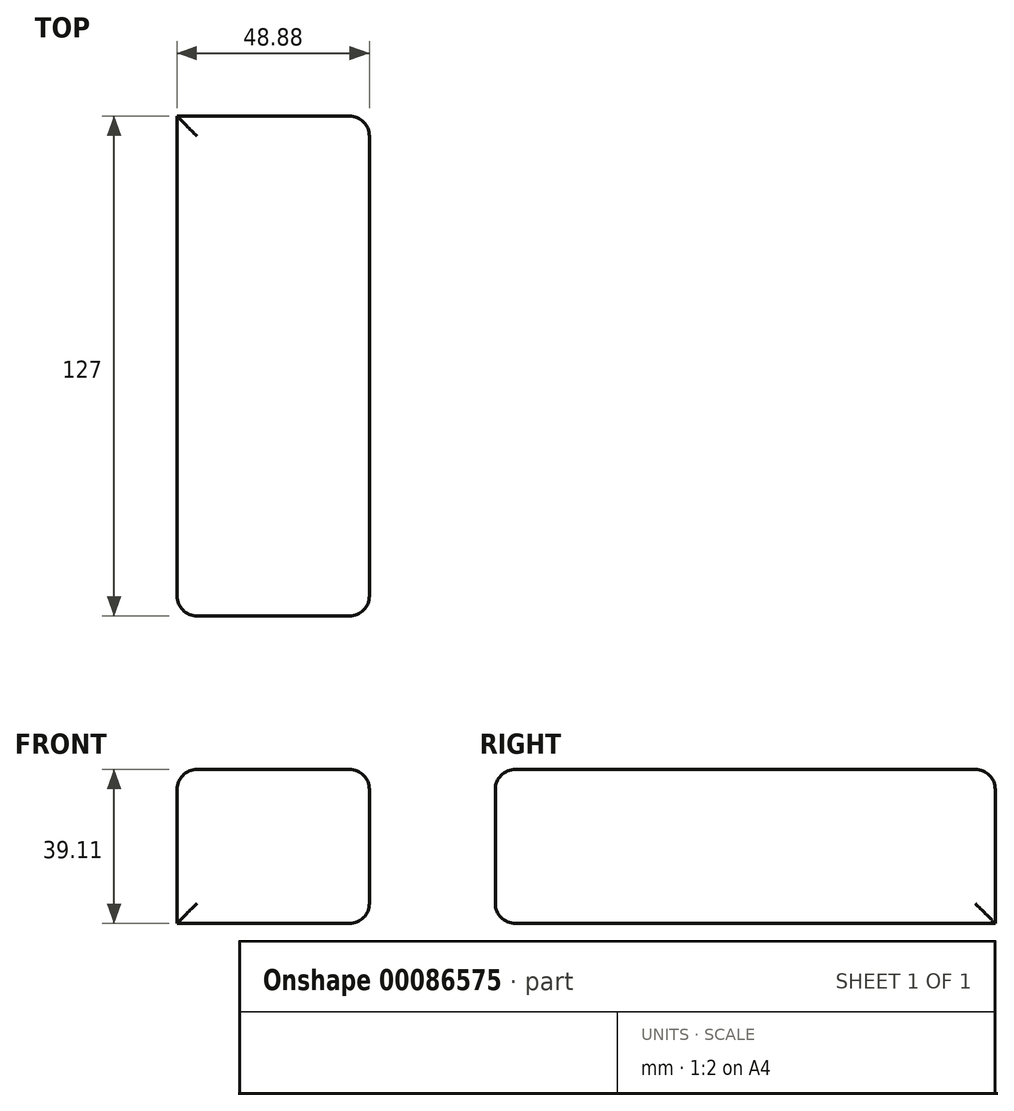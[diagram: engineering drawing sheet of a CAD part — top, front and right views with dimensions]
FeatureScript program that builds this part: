
annotation { "Feature Type Name" : "Feature", "Feature Type Description" : "" }
export const myFeature = defineFeature(function(context is Context, id is Id, definition is map)
    precondition{}
    {
        {
            var Q0;
            Q0=qCreatedBy(makeId("Front.planeOp"),FACE);
            var sketch = newSketch(context, id + "F0", { "sketchPlane" : qUnion([Q0])});
            skLineSegment(sketch, "E0.bottom", {"start": v(-132.52, 62.5) * mm, "end": v(-83.64, 62.5) * mm});
            skLineSegment(sketch, "E0.top", {"start": v(-132.52, 23.38) * mm, "end": v(-83.64, 23.38) * mm});
            skLineSegment(sketch, "E0.left", {"start": v(-132.52, 62.5) * mm, "end": v(-132.52, 23.38) * mm});
            skLineSegment(sketch, "E0.right", {"start": v(-83.64, 62.5) * mm, "end": v(-83.64, 23.38) * mm});
            skSolve(sketch);
        }
        {
            var Q0;
            Q0 = qSketchRegion(id + "F0", true);
            var Q1;
            Q1=makeQuery(id+"F0.imprint","IMPRINT",FACE,{"disambiguationData":[TD([[makeQuery(id+"F0.imprint","IMPRINT",EDGE,{"derivedFrom":sQuery(id+"F0.wireOp",EDGE,"E0.bottom")}),-1.0]])]});
            extrude(context, id + "F1", {"entities" : qUnion([Q0, Q1]), "depth" : 127 * mm});
        }
        {
            var Q0;
            Q0=makeQuery(id+"F1.opExtrude","CAP_EDGE",EDGE,{"disambiguationData":[OSD([sQuery(id+"F0.wireOp",EDGE,"E0.bottom")])],"isStart":false});
            var Q1;
            Q1=makeQuery(id+"F1.opExtrude","SWEPT_EDGE",EDGE,{"disambiguationData":[OSD([sQuery(id+"F0.wireOp",EDGE,"E0.bottom"),sQuery(id+"F0.wireOp",EDGE,"E0.right")])]});
            var Q2;
            Q2=makeQuery(id+"F1.opExtrude","CAP_EDGE",EDGE,{"disambiguationData":[OSD([sQuery(id+"F0.wireOp",EDGE,"E0.bottom")])],"isStart":true});
            var Q3;
            Q3=makeQuery(id+"F1.opExtrude","SWEPT_EDGE",EDGE,{"disambiguationData":[OSD([sQuery(id+"F0.wireOp",EDGE,"E0.bottom"),sQuery(id+"F0.wireOp",EDGE,"E0.left")])]});
            var Q4;
            Q4=makeQuery(id+"F1.opExtrude","SWEPT_EDGE",EDGE,{"disambiguationData":[OSD([sQuery(id+"F0.wireOp",EDGE,"E0.top"),sQuery(id+"F0.wireOp",EDGE,"E0.right")])]});
            var Q5;
            Q5=makeQuery(id+"F1.opExtrude","CAP_EDGE",EDGE,{"disambiguationData":[OSD([sQuery(id+"F0.wireOp",EDGE,"E0.top")])],"isStart":false});
            var Q6;
            Q6=makeQuery(id+"F1.opExtrude","CAP_EDGE",EDGE,{"disambiguationData":[OSD([sQuery(id+"F0.wireOp",EDGE,"E0.left")])],"isStart":false});
            var Q7;
            Q7=makeQuery(id+"F1.opExtrude","CAP_FACE",FACE,{"disambiguationData":[OSD([sQuery(id+"F0.wireOp",EDGE,"E0.bottom"),sQuery(id+"F0.wireOp",EDGE,"E0.top"),sQuery(id+"F0.wireOp",EDGE,"E0.left"),sQuery(id+"F0.wireOp",EDGE,"E0.right")])],"isStart":false});
            var Q8;
            Q8=makeQuery(id+"F1.opExtrude","CAP_EDGE",EDGE,{"disambiguationData":[OSD([sQuery(id+"F0.wireOp",EDGE,"E0.right")])],"isStart":false});
            var Q9;
            Q9=makeQuery(id+"F1.opExtrude","CAP_EDGE",EDGE,{"disambiguationData":[OSD([sQuery(id+"F0.wireOp",EDGE,"E0.right")])],"isStart":true});
            fillet(context, id + "F2", {"entities" : qUnion([Q0, Q1, Q2, Q3, Q4, Q5, Q6, Q7, Q8, Q9]), "radius" : 5.08 * mm, "tangentPropagation" : true, "allowEdgeOverflow" : false});
        }
    });
